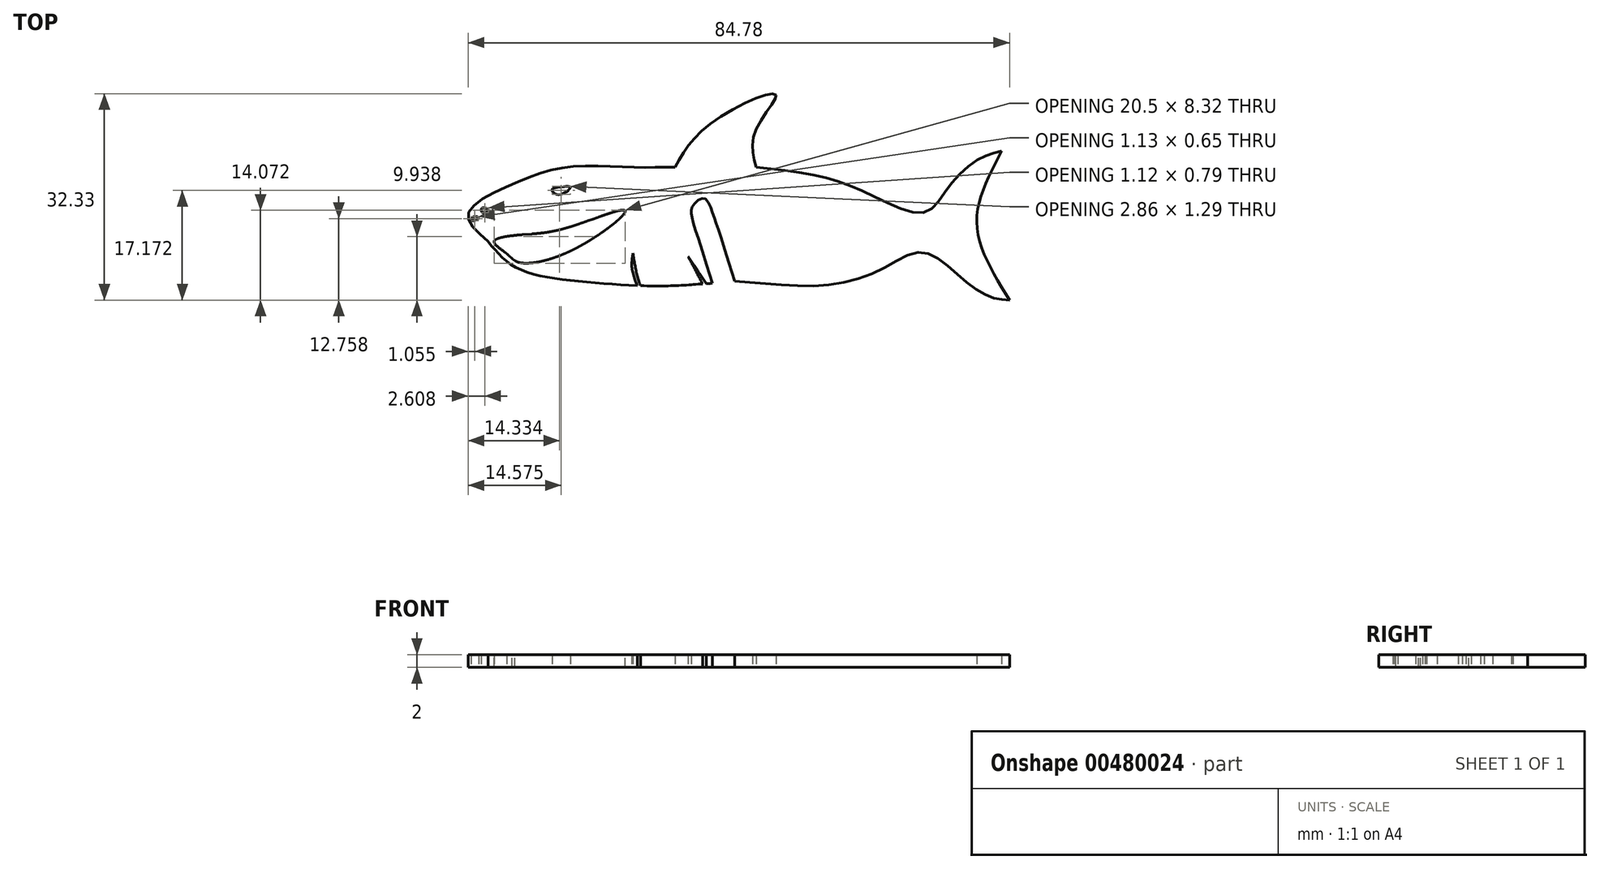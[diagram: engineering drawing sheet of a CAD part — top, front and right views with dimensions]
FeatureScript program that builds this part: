
annotation { "Feature Type Name" : "Feature", "Feature Type Description" : "" }
export const myFeature = defineFeature(function(context is Context, id is Id, definition is map)
    precondition{}
    {
        {
            var Q0;
            Q0=qCreatedBy(makeId("Top.planeOp"),FACE);
            var sketch = newSketch(context, id + "F0", { "sketchPlane" : qUnion([Q0])});
            skFitSpline(sketch, "E0", {"points": [v(-45.7, -6.22) * mm, v(-41.39, -10.24) * mm, v(-31.25, -12.46) * mm, v(-17.79, -13.16) * mm, v(-10.57, -12.75) * mm], "startDerivative": vector(17.94, -22.16) * mm, "endDerivative": vector(28.15, 1.12) * mm});
            skFitSpline(sketch, "E1", {"points": [v(-7.1, -12.43) * mm, v(4.98, -13.16) * mm, v(15.4, -10.8) * mm, v(22.2, -7.88) * mm, v(27.61, -11.21) * mm, v(32.75, -14.82) * mm, v(35.94, -15.38) * mm], "startDerivative": vector(53.2, -1.91) * mm, "endDerivative": vector(27.64, -1.33) * mm});
            skFitSpline(sketch, "E2", {"points": [v(35.94, -15.38) * mm, v(30.8, -3.44) * mm, v(34.7, 7.95) * mm], "startDerivative": vector(-14.67, 23.48) * mm, "endDerivative": vector(12.34, 23.17) * mm});
            skFitSpline(sketch, "E3", {"points": [v(34.7, 7.95) * mm, v(31.08, 6.7) * mm, v(26.22, 2.11) * mm, v(22.62, -1.63) * mm, v(14.7, 0.87) * mm, v(6.51, 3.92) * mm, v(-3.76, 5.45) * mm], "startDerivative": vector(-28.6, -6.41) * mm, "endDerivative": vector(-52.89, 5.7) * mm});
            skFitSpline(sketch, "E4", {"points": [v(-3.76, 5.45) * mm, v(-3.76, 11.35) * mm, v(-0.67, 16.8) * mm, v(-10.66, 12.42) * mm, v(-16.44, 5.45) * mm], "startDerivative": vector(-6.75, 25.84) * mm, "endDerivative": vector(-14.37, -25.94) * mm});
            skFitSpline(sketch, "E5", {"points": [v(-16.44, 5.45) * mm, v(-23.54, 5.45) * mm, v(-33.36, 5.45) * mm, v(-41.87, 2.76) * mm, v(-48.8, -1.86) * mm, v(-45.7, -6.22) * mm], "startDerivative": vector(-35.2, -0.7) * mm, "endDerivative": vector(31.06, -26.87) * mm});
            skFitSpline(sketch, "E6", {"points": [v(-44.75, -6.22) * mm, v(-42.77, -8.13) * mm, v(-40.96, -9.45) * mm, v(-32.2, -7.4) * mm, v(-24.28, -1.36) * mm, v(-33.2, -4) * mm, v(-40.63, -5.16) * mm, v(-44.75, -6.22) * mm]});
            skFitSpline(sketch, "E7", {"points": [v(-10.57, -12.75) * mm, v(-13.9, -1.72) * mm, v(-13.58, -0.5) * mm, v(-11.9, 0.57) * mm, v(-10.61, -1.56) * mm, v(-7.1, -12.43) * mm], "startDerivative": vector(-22.2, 71.64) * mm, "endDerivative": vector(22.76, -73.47) * mm});
            skLineSegment(sketch, "E8", {"start": v(-39.97, -9.6) * mm, "end": v(-39.55, -8.42) * mm});
            skLineSegment(sketch, "E9", {"start": v(-39.55, -8.42) * mm, "end": v(-38.88, -9.56) * mm});
            skLineSegment(sketch, "E10", {"start": v(-38.88, -9.56) * mm, "end": v(-38.5, -8.27) * mm});
            skLineSegment(sketch, "E11", {"start": v(-38.5, -8.27) * mm, "end": v(-37.68, -9.37) * mm});
            skLineSegment(sketch, "E12", {"start": v(-37.68, -9.37) * mm, "end": v(-37.39, -8) * mm});
            skLineSegment(sketch, "E13", {"start": v(-37.39, -8) * mm, "end": v(-36.46, -9.07) * mm});
            skLineSegment(sketch, "E14", {"start": v(-36.46, -9.07) * mm, "end": v(-36.46, -7.83) * mm});
            skLineSegment(sketch, "E15", {"start": v(-36.46, -7.83) * mm, "end": v(-35.49, -8.77) * mm});
            skLineSegment(sketch, "E16", {"start": v(-35.49, -8.77) * mm, "end": v(-35.49, -7.54) * mm});
            skLineSegment(sketch, "E17", {"start": v(-35.49, -7.54) * mm, "end": v(-34.59, -8.45) * mm});
            skLineSegment(sketch, "E18", {"start": v(-34.59, -8.45) * mm, "end": v(-34.35, -7.16) * mm});
            skLineSegment(sketch, "E19", {"start": v(-34.35, -7.16) * mm, "end": v(-33.72, -8.1) * mm});
            skLineSegment(sketch, "E20", {"start": v(-33.72, -8.1) * mm, "end": v(-33.45, -6.84) * mm});
            skLineSegment(sketch, "E21", {"start": v(-33.45, -6.84) * mm, "end": v(-32.8, -7.68) * mm});
            skLineSegment(sketch, "E22", {"start": v(-32.8, -7.68) * mm, "end": v(-32.51, -6.58) * mm});
            skLineSegment(sketch, "E23", {"start": v(-32.51, -6.58) * mm, "end": v(-32, -7.28) * mm});
            skLineSegment(sketch, "E24", {"start": v(-32, -7.28) * mm, "end": v(-32, -6.26) * mm});
            skLineSegment(sketch, "E25", {"start": v(-32, -6.26) * mm, "end": v(-31.38, -6.96) * mm});
            skLineSegment(sketch, "E26", {"start": v(-31.38, -6.96) * mm, "end": v(-31.23, -6.11) * mm});
            skLineSegment(sketch, "E27", {"start": v(-31.23, -6.11) * mm, "end": v(-30.79, -6.62) * mm});
            skLineSegment(sketch, "E28", {"start": v(-30.79, -6.62) * mm, "end": v(-30.59, -5.73) * mm});
            skLineSegment(sketch, "E29", {"start": v(-30.59, -5.73) * mm, "end": v(-30.16, -6.26) * mm});
            skLineSegment(sketch, "E30", {"start": v(-30.16, -6.26) * mm, "end": v(-30.16, -5.32) * mm});
            skLineSegment(sketch, "E31", {"start": v(-30.16, -5.32) * mm, "end": v(-29.47, -5.83) * mm});
            skLineSegment(sketch, "E32", {"start": v(-29.47, -5.83) * mm, "end": v(-29.47, -5) * mm});
            skLineSegment(sketch, "E33", {"start": v(-29.47, -5) * mm, "end": v(-28.96, -5.51) * mm});
            skLineSegment(sketch, "E34", {"start": v(-28.96, -5.51) * mm, "end": v(-28.96, -4.62) * mm});
            skLineSegment(sketch, "E35", {"start": v(-28.96, -4.62) * mm, "end": v(-28.29, -5.06) * mm});
            skLineSegment(sketch, "E36", {"start": v(-28.29, -5.06) * mm, "end": v(-28.29, -4.21) * mm});
            skLineSegment(sketch, "E37", {"start": v(-28.29, -4.21) * mm, "end": v(-27.55, -4.55) * mm});
            skLineSegment(sketch, "E38", {"start": v(-27.55, -4.55) * mm, "end": v(-27.55, -3.75) * mm});
            skLineSegment(sketch, "E39", {"start": v(-27.55, -3.75) * mm, "end": v(-26.93, -4.1) * mm});
            skLineSegment(sketch, "E40", {"start": v(-26.93, -4.1) * mm, "end": v(-26.9, -3.3) * mm});
            skLineSegment(sketch, "E41", {"start": v(-26.9, -3.3) * mm, "end": v(-26.3, -3.62) * mm});
            skLineSegment(sketch, "E42", {"start": v(-26.3, -3.62) * mm, "end": v(-26.3, -2.87) * mm});
            skLineSegment(sketch, "E43", {"start": v(-26.3, -2.87) * mm, "end": v(-25.8, -3.22) * mm});
            skLineSegment(sketch, "E44", {"start": v(-25.8, -3.22) * mm, "end": v(-25.8, -2.5) * mm});
            skLineSegment(sketch, "E45", {"start": v(-25.8, -2.5) * mm, "end": v(-25.32, -2.8) * mm});
            skLineSegment(sketch, "E46", {"start": v(-25.32, -2.8) * mm, "end": v(-25.32, -2.26) * mm});
            skLineSegment(sketch, "E47", {"start": v(-25.32, -2.26) * mm, "end": v(-24.76, -2.26) * mm});
            skLineSegment(sketch, "E48", {"start": v(-41.77, -5.27) * mm, "end": v(-40.63, -6.72) * mm});
            skLineSegment(sketch, "E49", {"start": v(-40.63, -6.72) * mm, "end": v(-40.35, -5.14) * mm});
            skLineSegment(sketch, "E50", {"start": v(-40.35, -5.14) * mm, "end": v(-39.26, -6.64) * mm});
            skLineSegment(sketch, "E51", {"start": v(-39.26, -6.64) * mm, "end": v(-38.86, -5.02) * mm});
            skLineSegment(sketch, "E52", {"start": v(-38.86, -5.02) * mm, "end": v(-37.77, -6.46) * mm});
            skLineSegment(sketch, "E53", {"start": v(-37.77, -6.46) * mm, "end": v(-37.4, -4.88) * mm});
            skLineSegment(sketch, "E54", {"start": v(-37.4, -4.88) * mm, "end": v(-36.2, -6.22) * mm});
            skLineSegment(sketch, "E55", {"start": v(-36.2, -6.22) * mm, "end": v(-36, -4.68) * mm});
            skLineSegment(sketch, "E56", {"start": v(-36, -4.68) * mm, "end": v(-35.14, -5.82) * mm});
            skLineSegment(sketch, "E57", {"start": v(-35.14, -5.82) * mm, "end": v(-34.86, -4.45) * mm});
            skLineSegment(sketch, "E58", {"start": v(-34.86, -4.45) * mm, "end": v(-33.97, -5.59) * mm});
            skLineSegment(sketch, "E59", {"start": v(-33.97, -5.59) * mm, "end": v(-33.74, -4.16) * mm});
            skLineSegment(sketch, "E60", {"start": v(-33.74, -4.16) * mm, "end": v(-32.78, -5.15) * mm});
            skLineSegment(sketch, "E61", {"start": v(-32.78, -5.15) * mm, "end": v(-32.78, -3.88) * mm});
            skLineSegment(sketch, "E62", {"start": v(-32.78, -3.88) * mm, "end": v(-31.73, -4.65) * mm});
            skLineSegment(sketch, "E63", {"start": v(-31.73, -4.65) * mm, "end": v(-31.73, -3.54) * mm});
            skLineSegment(sketch, "E64", {"start": v(-31.73, -3.54) * mm, "end": v(-30.9, -4.36) * mm});
            skLineSegment(sketch, "E65", {"start": v(-30.9, -4.36) * mm, "end": v(-30.81, -3.22) * mm});
            skLineSegment(sketch, "E66", {"start": v(-30.81, -3.22) * mm, "end": v(-30.1, -3.9) * mm});
            skLineSegment(sketch, "E67", {"start": v(-30.1, -3.9) * mm, "end": v(-30.1, -2.97) * mm});
            skLineSegment(sketch, "E68", {"start": v(-30.1, -2.97) * mm, "end": v(-29.27, -3.63) * mm});
            skLineSegment(sketch, "E69", {"start": v(-29.27, -3.63) * mm, "end": v(-29.27, -2.68) * mm});
            skLineSegment(sketch, "E70", {"start": v(-29.27, -2.68) * mm, "end": v(-28.54, -3.2) * mm});
            skLineSegment(sketch, "E71", {"start": v(-28.54, -3.2) * mm, "end": v(-28.54, -2.42) * mm});
            skLineSegment(sketch, "E72", {"start": v(-28.54, -2.42) * mm, "end": v(-27.9, -2.93) * mm});
            skLineSegment(sketch, "E73", {"start": v(-27.9, -2.93) * mm, "end": v(-27.9, -2.2) * mm});
            skLineSegment(sketch, "E74", {"start": v(-27.9, -2.2) * mm, "end": v(-27.35, -2.6) * mm});
            skLineSegment(sketch, "E75", {"start": v(-27.35, -2.6) * mm, "end": v(-27.35, -2) * mm});
            skLineSegment(sketch, "E76", {"start": v(-27.35, -2) * mm, "end": v(-26.9, -2.3) * mm});
            skLineSegment(sketch, "E77", {"start": v(-26.9, -2.3) * mm, "end": v(-26.9, -1.85) * mm});
            skLineSegment(sketch, "E78", {"start": v(-26.9, -1.85) * mm, "end": v(-26.57, -2.1) * mm});
            skLineSegment(sketch, "E79", {"start": v(-26.57, -2.1) * mm, "end": v(-26.37, -1.68) * mm});
            skLineSegment(sketch, "E80", {"start": v(-41.77, -5.27) * mm, "end": v(-41.77, -7.12) * mm});
            skLineSegment(sketch, "E81", {"start": v(-41.77, -7.12) * mm, "end": v(-42.91, -5.43) * mm});
            skLineSegment(sketch, "E82", {"start": v(-42.91, -5.43) * mm, "end": v(-42.91, -6.98) * mm});
            skLineSegment(sketch, "E83", {"start": v(-42.91, -6.98) * mm, "end": v(-44.1, -5.71) * mm});
            skLineSegment(sketch, "E84", {"start": v(-39.97, -9.6) * mm, "end": v(-40.43, -8.52) * mm});
            skLineSegment(sketch, "E85", {"start": v(-40.43, -8.52) * mm, "end": v(-40.96, -9.45) * mm});
            skLineSegment(sketch, "E86", {"start": v(-40.96, -9.45) * mm, "end": v(-41.24, -8.56) * mm});
            skLineSegment(sketch, "E87", {"start": v(-41.24, -8.56) * mm, "end": v(-41.54, -9.19) * mm});
            skLineSegment(sketch, "E88", {"start": v(-41.54, -9.19) * mm, "end": v(-41.87, -8.66) * mm});
            skLineSegment(sketch, "E89", {"start": v(-41.87, -8.66) * mm, "end": v(-41.95, -8.88) * mm});
            skFitSpline(sketch, "E90", {"points": [v(-34.23, 2.35) * mm, v(-35.69, 1.94) * mm, v(-34.76, 1.12) * mm, v(-32.83, 2.29) * mm, v(-34.23, 2.35) * mm]});
            skFitSpline(sketch, "E91", {"points": [v(-45.67, -1.27) * mm, v(-46.66, -0.98) * mm, v(-46.55, -1.68) * mm, v(-45.67, -1.27) * mm]});
            skFitSpline(sketch, "E92", {"points": [v(-47.95, -2.32) * mm, v(-48.3, -2.9) * mm, v(-47.19, -2.56) * mm, v(-47.95, -2.32) * mm]});
            skFitSpline(sketch, "E93", {"points": [v(-23.03, -8.03) * mm, v(-20.77, -15) * mm, v(-13.6, -19.72) * mm, v(-9.78, -20.2) * mm, v(-14.39, -8.52) * mm], "startDerivative": vector(4.67, -30.85) * mm, "endDerivative": vector(-25.89, 49.06) * mm});
            skFitSpline(sketch, "E94", {"points": [v(-22.37, -13.1) * mm, v(-23.19, -10.34) * mm, v(-23.03, -8.03) * mm], "startDerivative": vector(-2.05, 5.2) * mm, "endDerivative": vector(0.78, 4.8) * mm});
            skFitSpline(sketch, "E95", {"points": [v(-11.56, -12.8) * mm, v(-14.39, -8.52) * mm], "startDerivative": vector(-2.85, 4.52) * mm, "endDerivative": vector(-2.85, 4.52) * mm});
            skFitSpline(sketch, "E96", {"points": [v(-41.95, -8.88) * mm, v(-42.77, -8.13) * mm, v(-44.75, -6.22) * mm, v(-44.1, -5.71) * mm], "startDerivative": vector(-2.04, 2.06) * mm, "endDerivative": vector(4.07, 1.49) * mm});
            skLineSegment(sketch, "E97", {"start": v(-10.57, -12.75) * mm, "end": v(-14.3, -0.73) * mm, "construction": true});
            skLineSegment(sketch, "E98", {"start": v(-7.1, -12.43) * mm, "end": v(-11.32, 1.2) * mm, "construction": true});
            skSolve(sketch);
        }
        {
            var Q0;
            Q0=makeQuery(id+"F0.imprint","IMPRINT",FACE,{"disambiguationData":[TD([[makeQuery(id+"F0.imprint","IMPRINT",EDGE,{"derivedFrom":sQuery(id+"F0.wireOp",EDGE,"E0")}),1.0]])]});
            extrude(context, id + "F1", {"entities" : qUnion([Q0]), "depth" : 2 * mm});
        }
    });
